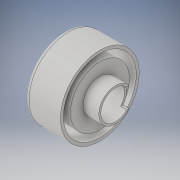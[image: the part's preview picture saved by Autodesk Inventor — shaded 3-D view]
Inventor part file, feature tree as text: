
AUTODESK INVENTOR PART (.ipt)
format: ipt  version: 2017 (Build 210142000, 142)  size: 219,136 bytes
history: native  units: in
note: dims shown in document units (in); Inventor stores cm internally (conversion verified against a paired STEP export)
features: extrude x5, sketch x5, fillet x2, plane x1, shell x1, projected_geometry x1
ambient origin geometry x8: Origin, YZ Plane, XZ Plane, XY Plane, X Axis, Y Axis, Z Axis, Center Point
bodies: Solid1 (feature_tree)
feature tree (15):
  plane  "Work Plane1"
  extrude  "Wheel"  Depth=0.5906in
  extrude  "Extrusion7"  Depth=0.7087in TaperAngle=0.0deg
  extrude  "Extrusion8"  Depth=0.0787in
  fillet  "Fillet1"  Radius=0.6693in
  fillet  "Fillet2"  Radius=0.1181in
  shell  "Shell1"  Thickness=0.0787in
  extrude  "Extrusion9"  Depth=0.0591in
  extrude  "Extrusion10"  Depth=0.315in TaperAngle=0.0deg
  sketch  "Sketch7"  dims[d0=0.7874in d28=0.5906in]
  sketch  "Sketch8"  dims[d29=1.5748in d30=0.7087in d31=0.0in]
  sketch  "Sketch9"  dims[d32=0.6693in d33=1.063in d34=0.6693in d35=0.0in d36=0.1181in d37=0.0in d38=0.0787in]
  sketch  "Sketch10"  dims[d39=0.0394in d40=0.0591in]
  sketch  "Sketch11"  dims[d41=0.6693in d42=0.315in d43=0.0in d44=0.1181in d45=0.3937in d46=0.1969in d47=0.7874in d48=0.0in]
  projected_geometry  "Projected Loop2"
